# Revit family: Specialty_Equipment-Planter-Planters_Unlimited-Modern-Lunetta Low Bowl Planter-rev
name_source: partatom
category: Specialty Equipment
units: mm (PartAtom-declared; Revit-internal decimal feet)

## family parameters
Always vertical = Yes
Cut with Voids When Loaded = No
Enable Cutting in Views = No
Maintain Annotation Orientation = No
OmniClass Number = 23.40.05.21.17
OmniClass Title = Planters
Part Type = Normal
Room Calculation Point = No
Round Connector Dimension = Use Diameter
Shared = No
Work Plane-Based = No

## types (5) — shared parameters
Assembly Code = G2050600
CD_Diameter = 0' - 0"
CD_Finish = Plastic-Fiberglass-Carlsbad-Semi_Gloss-Charcoal
CD_Microsite = https://www.caddetails.com
CD_Offset = 0' - 0 1/2"
CD_Product Page URL = https://www.plantersunlimited.com
CD_Specification = https://www.plantersunlimited.com
Default Elevation = 0' - 0"
Description = Modular Planting Bed
Manufacturer = Planters Unlimited
Model = Lunetta Fiberglass Low Bowl Planter
Type Comments = Round Planter
URL = https://www.plantersunlimited.com

## per-type parameters (varying)
| type | Base thickness | CD_Diameter Min | CD_Height | CD_Width |
| 24" Dia x 8"H | 0' - 2" | 1' - 0" | 0' - 8" | 2' - 0" |
| 29" Dia x 10"H | 0' - 2 1/2" | 1' - 2 1/2" | 0' - 10" | 2' - 5" |
| 32" Dia x 11"H | 0' - 2 1/2" | 1' - 4" | 0' - 11" | 2' - 8" |
| 36" Dia x 11"H | 0' - 2 1/2" | 1' - 6" | 0' - 11" | 3' - 0" |
| 47" Dia x 11"H | 0' - 2 1/2" | 1' - 11 1/2" | 0' - 11" | 3' - 11" |

## geometry (parser evidence)
native form markers: Sweep x3
no freeform markers — native parametric forms only
